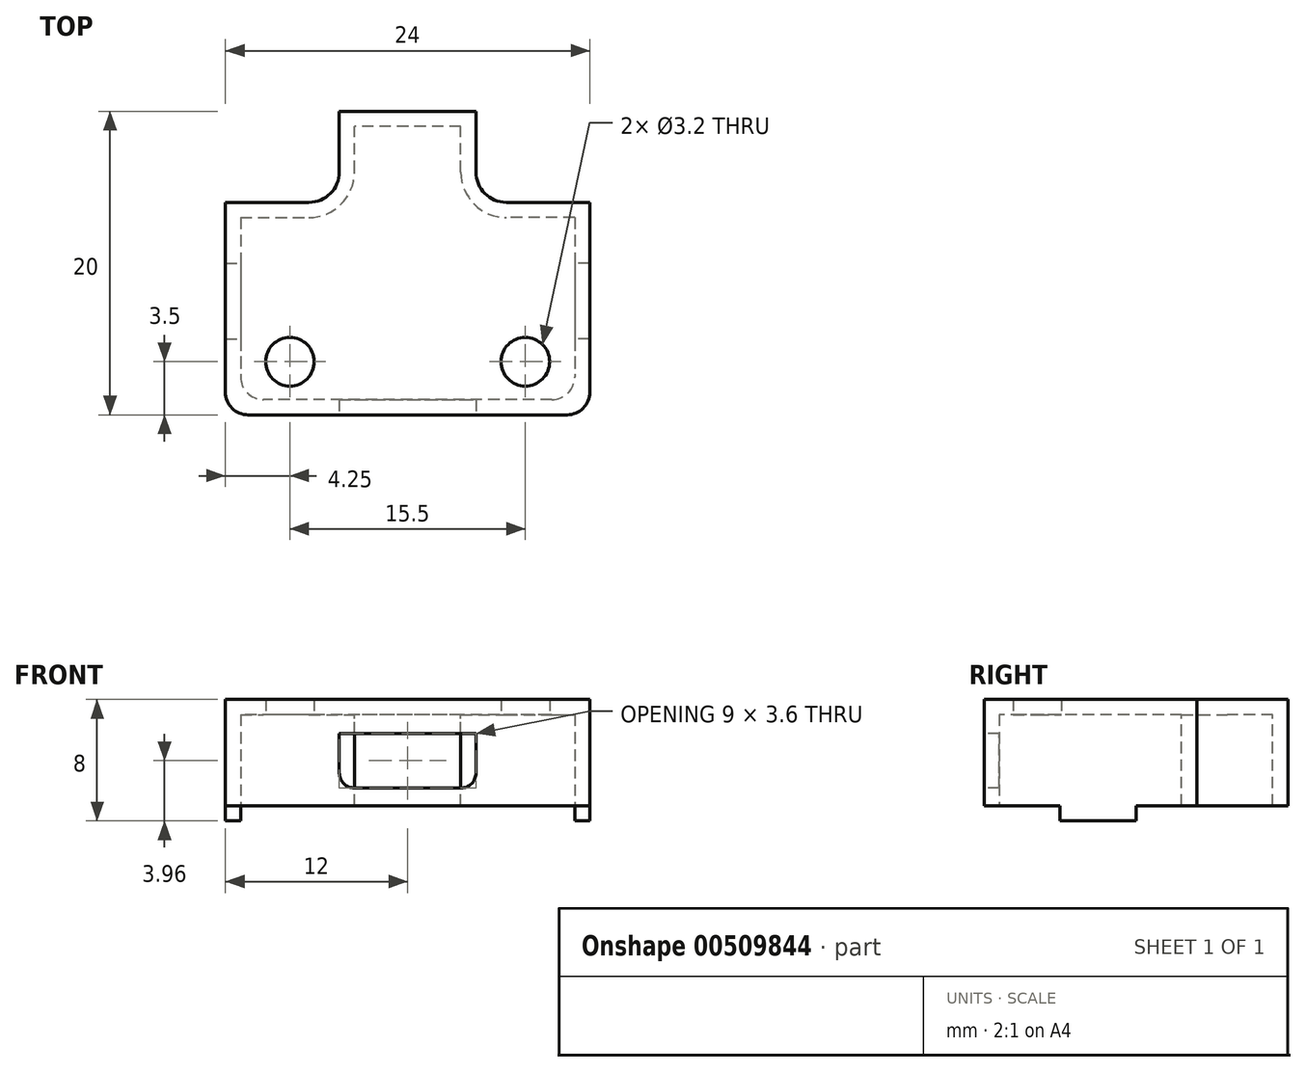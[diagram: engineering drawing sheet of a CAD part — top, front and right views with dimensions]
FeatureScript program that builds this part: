
annotation { "Feature Type Name" : "Feature", "Feature Type Description" : "" }
export const myFeature = defineFeature(function(context is Context, id is Id, definition is map)
    precondition{}
    {
        {
            var Q0;
            Q0=qCreatedBy(makeId("Top.planeOp"),FACE);
            var sketch = newSketch(context, id + "F0", { "sketchPlane" : qUnion([Q0])});
            skLineSegment(sketch, "E0.bottom", {"start": v(12, 2.5) * mm, "end": v(-12, 2.5) * mm});
            skLineSegment(sketch, "E0.top", {"start": v(12, -2.5) * mm, "end": v(-12, -2.5) * mm});
            skLineSegment(sketch, "E0.left", {"start": v(12, 2.5) * mm, "end": v(12, -2.5) * mm});
            skLineSegment(sketch, "E0.right", {"start": v(-12, 2.5) * mm, "end": v(-12, -2.5) * mm});
            skPoint(sketch, "E0.middle", {"position": v(0, 0) * mm});
            skCircle(sketch, "E1", {"center": v(-7, 0) * mm, "radius": 1.7 * mm});
            skCircle(sketch, "E2", {"center": v(7, 0) * mm, "radius": 1.7 * mm});
            skPoint(sketch, "E3.center.orphan", {"position": v(-2.5, 0) * mm});
            skPoint(sketch, "E4.center.orphan", {"position": v(-0.83, 0) * mm});
            skPoint(sketch, "E5.center.orphan", {"position": v(0.83, 0) * mm});
            skPoint(sketch, "E6.center.orphan", {"position": v(2.5, 0) * mm});
            skSolve(sketch);
        }
        {
            var Q0;
            Q0=qSketchRegion(id+"F0",true);
            extrude(context, id + "F1", {"entities" : qUnion([Q0]), "depth" : 7 * mm});
        }
        {
            var Q0;
            Q0=makeQuery(id+"F1.opExtrude","SWEPT_FACE",FACE,{"disambiguationData":[OSD([sQuery(id+"F0.wireOp",EDGE,"E0.top")])]});
            var sketch = newSketch(context, id + "F2", { "sketchPlane" : qUnion([Q0])});
            skLineSegment(sketch, "E7.bottom", {"start": v(-12, 7) * mm, "end": v(12, 7) * mm});
            skLineSegment(sketch, "E7.top", {"start": v(-12, 0) * mm, "end": v(12, 0) * mm});
            skLineSegment(sketch, "E7.left", {"start": v(-12, 7) * mm, "end": v(-12, 0) * mm});
            skLineSegment(sketch, "E7.right", {"start": v(12, 7) * mm, "end": v(12, 0) * mm});
            skSolve(sketch);
        }
        {
            var Q0;
            Q0=qSketchRegion(id+"F2",true);
            extrude(context, id + "F3", {"entities" : qUnion([Q0]), "operationType" : NewBodyOperationType.ADD, "depth" : 15 * mm});
        }
        {
            var Q0;
            Q0=makeQuery(id+"F3.boolean.opBoolean","MERGE",FACE,{"derivedFrom":[makeQuery(id+"F1.opExtrude","CAP_FACE",FACE,{"disambiguationData":[OSD([sQuery(id+"F0.wireOp",EDGE,"E0.bottom"),sQuery(id+"F0.wireOp",EDGE,"E0.top"),sQuery(id+"F0.wireOp",EDGE,"E0.left"),sQuery(id+"F0.wireOp",EDGE,"E0.right"),sQuery(id+"F0.wireOp",EDGE,"E3"),sQuery(id+"F0.wireOp",EDGE,"E4"),sQuery(id+"F0.wireOp",EDGE,"E5"),sQuery(id+"F0.wireOp",EDGE,"E6"),sQuery(id+"F0.wireOp",EDGE,"E1"),sQuery(id+"F0.wireOp",EDGE,"E2")])],"isStart":true}),makeQuery(id+"F3.opExtrude","SWEPT_FACE",FACE,{"disambiguationData":[OSD([sQuery(id+"F2.wireOp",EDGE,"E7.top")])]})]});
            var sketch = newSketch(context, id + "F4", { "sketchPlane" : qUnion([Q0])});
            skCircle(sketch, "E8", {"center": v(-7.75, 14) * mm, "radius": 1.6 * mm});
            skCircle(sketch, "E9", {"center": v(7.75, 14) * mm, "radius": 1.6 * mm});
            skSolve(sketch);
        }
        {
            var Q0;
            Q0=qSketchRegion(id+"F4",true);
            extrude(context, id + "F5", {"entities" : qUnion([Q0]), "operationType" : NewBodyOperationType.REMOVE, "oppositeDirection" : true, "depth" : 25 * mm});
        }
        {
            var Q0;
            Q0=makeQuery(id+"F3.boolean.opBoolean","MERGE",FACE,{"derivedFrom":[makeQuery(id+"F1.opExtrude","CAP_FACE",FACE,{"disambiguationData":[OSD([sQuery(id+"F0.wireOp",EDGE,"E0.bottom"),sQuery(id+"F0.wireOp",EDGE,"E0.top"),sQuery(id+"F0.wireOp",EDGE,"E0.left"),sQuery(id+"F0.wireOp",EDGE,"E0.right"),sQuery(id+"F0.wireOp",EDGE,"E3"),sQuery(id+"F0.wireOp",EDGE,"E4"),sQuery(id+"F0.wireOp",EDGE,"E5"),sQuery(id+"F0.wireOp",EDGE,"E6"),sQuery(id+"F0.wireOp",EDGE,"E1"),sQuery(id+"F0.wireOp",EDGE,"E2")])],"isStart":false}),makeQuery(id+"F3.opExtrude","SWEPT_FACE",FACE,{"disambiguationData":[OSD([sQuery(id+"F2.wireOp",EDGE,"E7.bottom")])]})]});
            var sketch = newSketch(context, id + "F6", { "sketchPlane" : qUnion([Q0])});
            skLineSegment(sketch, "E10", {"start": v(-12, 2.5) * mm, "end": v(-4.5, 2.5) * mm});
            skLineSegment(sketch, "E11", {"start": v(-12, 2.5) * mm, "end": v(-12, -3.5) * mm});
            skLineSegment(sketch, "E12", {"start": v(12, 2.5) * mm, "end": v(4.5, 2.5) * mm});
            skLineSegment(sketch, "E13", {"start": v(12, 2.5) * mm, "end": v(12, -3.5) * mm});
            skLineSegment(sketch, "E14", {"start": v(4.5, 2.5) * mm, "end": v(4.5, -1.5) * mm});
            skLineSegment(sketch, "E15", {"start": v(6.5, -3.5) * mm, "end": v(12, -3.5) * mm});
            skLineSegment(sketch, "E16", {"start": v(-4.5, 2.5) * mm, "end": v(-4.5, -1.5) * mm});
            skLineSegment(sketch, "E17", {"start": v(-6.5, -3.5) * mm, "end": v(-12, -3.5) * mm});
            skPoint(sketch, "E18.visualSharp", {"position": v(4.5, -3.5) * mm});
            skArc(sketch, "E18.filletArc", {"start": v(4.5, -1.5) * mm, "mid": v(5.09, -2.91) * mm, "end": v(6.5, -3.5) * mm});
            skPoint(sketch, "E19.visualSharp", {"position": v(-4.5, -3.5) * mm});
            skArc(sketch, "E19.filletArc", {"start": v(-6.5, -3.5) * mm, "mid": v(-5.09, -2.91) * mm, "end": v(-4.5, -1.5) * mm});
            skPoint(sketch, "E20.visualSharp", {"position": v(12, -3.5) * mm});
            skSolve(sketch);
        }
        {
            var Q0;
            Q0 = qSketchRegion(id + "F6", true);
            var Q1;
            Q1=makeQuery(id+"F3.boolean.opBoolean","MERGE",FACE,{"derivedFrom":[makeQuery(id+"F1.opExtrude","CAP_FACE",FACE,{"disambiguationData":[OSD([sQuery(id+"F0.wireOp",EDGE,"E0.bottom"),sQuery(id+"F0.wireOp",EDGE,"E0.top"),sQuery(id+"F0.wireOp",EDGE,"E0.left"),sQuery(id+"F0.wireOp",EDGE,"E0.right"),sQuery(id+"F0.wireOp",EDGE,"E3"),sQuery(id+"F0.wireOp",EDGE,"E4"),sQuery(id+"F0.wireOp",EDGE,"E5"),sQuery(id+"F0.wireOp",EDGE,"E6"),sQuery(id+"F0.wireOp",EDGE,"E1"),sQuery(id+"F0.wireOp",EDGE,"E2")])],"isStart":true}),makeQuery(id+"F3.opExtrude","SWEPT_FACE",FACE,{"disambiguationData":[OSD([sQuery(id+"F2.wireOp",EDGE,"E7.top")])]})]});
            extrude(context, id + "F7", {"entities" : qUnion([Q0]), "operationType" : NewBodyOperationType.REMOVE, "endBound" : BoundingType.UP_TO_SURFACE, "oppositeDirection" : true, "endBoundEntityFace" : qUnion([Q1]), "depth" : 25 * mm});
        }
        {
            var Q0;
            Q0=makeQuery(id+"F3.boolean.opBoolean","MERGE",FACE,{"derivedFrom":[makeQuery(id+"F1.opExtrude","CAP_FACE",FACE,{"disambiguationData":[OSD([sQuery(id+"F0.wireOp",EDGE,"E0.bottom"),sQuery(id+"F0.wireOp",EDGE,"E0.top"),sQuery(id+"F0.wireOp",EDGE,"E0.left"),sQuery(id+"F0.wireOp",EDGE,"E0.right"),sQuery(id+"F0.wireOp",EDGE,"E1"),sQuery(id+"F0.wireOp",EDGE,"E2")])],"isStart":true}),makeQuery(id+"F3.opExtrude","SWEPT_FACE",FACE,{"disambiguationData":[OSD([sQuery(id+"F2.wireOp",EDGE,"E7.top")])]})]});
            shell(context, id + "F8", {"entities" : qUnion([Q0]), "thickness" : 1 * mm});
        }
        {
            var Q0;
            Q0=makeQuery(id+"F3.boolean.opBoolean","MERGE",FACE,{"derivedFrom":[makeQuery(id+"F1.opExtrude","CAP_FACE",FACE,{"disambiguationData":[OSD([sQuery(id+"F0.wireOp",EDGE,"E0.bottom"),sQuery(id+"F0.wireOp",EDGE,"E0.top"),sQuery(id+"F0.wireOp",EDGE,"E0.left"),sQuery(id+"F0.wireOp",EDGE,"E0.right"),sQuery(id+"F0.wireOp",EDGE,"E1"),sQuery(id+"F0.wireOp",EDGE,"E2")])],"isStart":true}),makeQuery(id+"F3.opExtrude","SWEPT_FACE",FACE,{"disambiguationData":[OSD([sQuery(id+"F2.wireOp",EDGE,"E7.top")])]})]});
            var sketch = newSketch(context, id + "F9", { "sketchPlane" : qUnion([Q0])});
            skLineSegment(sketch, "E21.bottom", {"start": v(-11, 16.5) * mm, "end": v(11, 16.5) * mm});
            skLineSegment(sketch, "E21.top", {"start": v(-11, 10.87) * mm, "end": v(11, 10.87) * mm});
            skLineSegment(sketch, "E21.left", {"start": v(-11, 16.5) * mm, "end": v(-11, 10.87) * mm});
            skLineSegment(sketch, "E21.right", {"start": v(11, 16.5) * mm, "end": v(11, 10.87) * mm});
            skSolve(sketch);
        }
        {
            var Q0;
            Q0 = qSketchRegion(id + "F9", true);
            var Q1;
            Q1=makeQuery(id+"F8.opShell","OFFSET_FACE",FACE,{"disambiguationData":[OSD([sQuery(id+"F0.wireOp",EDGE,"E0.bottom"),sQuery(id+"F0.wireOp",EDGE,"E0.top"),sQuery(id+"F0.wireOp",EDGE,"E0.left"),sQuery(id+"F0.wireOp",EDGE,"E0.right"),sQuery(id+"F0.wireOp",EDGE,"E1"),sQuery(id+"F0.wireOp",EDGE,"E2"),sQuery(id+"F2.wireOp",EDGE,"E7.bottom")])]});
            extrude(context, id + "F10", {"entities" : qUnion([Q0]), "operationType" : NewBodyOperationType.REMOVE, "endBound" : BoundingType.UP_TO_SURFACE, "oppositeDirection" : true, "endBoundEntityFace" : qUnion([Q1]), "depth" : 25 * mm});
        }
        {
            var Q0;
            Q0=makeQuery(id+"F3.opExtrude","CAP_FACE",FACE,{"disambiguationData":[OSD([sQuery(id+"F2.wireOp",EDGE,"E7.bottom"),sQuery(id+"F2.wireOp",EDGE,"E7.top"),sQuery(id+"F2.wireOp",EDGE,"E7.left"),sQuery(id+"F2.wireOp",EDGE,"E7.right")])],"isStart":false});
            var sketch = newSketch(context, id + "F11", { "sketchPlane" : qUnion([Q0])});
            skLineSegment(sketch, "E22.bottom", {"start": v(4.5, 4.76) * mm, "end": v(-4.5, 4.76) * mm});
            skLineSegment(sketch, "E22.top", {"start": v(4.5, 1.16) * mm, "end": v(-4.5, 1.16) * mm});
            skLineSegment(sketch, "E22.left", {"start": v(4.5, 4.76) * mm, "end": v(4.5, 1.16) * mm});
            skLineSegment(sketch, "E22.right", {"start": v(-4.5, 4.76) * mm, "end": v(-4.5, 1.16) * mm});
            skPoint(sketch, "E22.middle", {"position": v(0, 2.96) * mm});
            skSolve(sketch);
        }
        {
            var Q0;
            Q0 = qSketchRegion(id + "F11", true);
            var Q1;
            {var subQ0=sQuery(id+"F2.wireOp",EDGE,"E7.right");var subQ1=sQuery(id+"F2.wireOp",EDGE,"E7.left");var subQ2=sQuery(id+"F2.wireOp",EDGE,"E7.top");var subQ3=sQuery(id+"F2.wireOp",EDGE,"E7.bottom");Q1=makeQuery(id+"F10.boolean.opBoolean","MERGE",FACE,{"derivedFrom":[makeQuery(id+"F8.opShell","OFFSET_FACE",FACE,{"disambiguationData":[OSD([subQ3,subQ2,subQ1,subQ0]),OD(0.0)]}),makeQuery(id+"F8.opShell","OFFSET_FACE",FACE,{"disambiguationData":[OSD([subQ3,subQ2,subQ1,subQ0]),OD(1.0)]}),makeQuery(id+"F8.opShell","OFFSET_FACE",FACE,{"disambiguationData":[OSD([subQ3,subQ2,subQ1,subQ0]),OD(2.0)]}),makeQuery(id+"F10.opExtrude","SWEPT_FACE",FACE,{"disambiguationData":[OSD([sQuery(id+"F9.wireOp",EDGE,"E21.bottom")])]})]});}
            extrude(context, id + "F12", {"entities" : qUnion([Q0]), "operationType" : NewBodyOperationType.REMOVE, "endBound" : BoundingType.UP_TO_SURFACE, "oppositeDirection" : true, "endBoundEntityFace" : qUnion([Q1]), "depth" : 25 * mm});
        }
        {
            var Q0;
            Q0=makeQuery(id+"F12.boolean.opBoolean","COPY",EDGE,{"derivedFrom":makeQuery(id+"F12.opExtrude","SWEPT_EDGE",EDGE,{"disambiguationData":[OSD([sQuery(id+"F11.wireOp",EDGE,"E22.top"),sQuery(id+"F11.wireOp",EDGE,"E22.right")])]})});
            var Q1;
            Q1=makeQuery(id+"F12.boolean.opBoolean","COPY",EDGE,{"derivedFrom":makeQuery(id+"F12.opExtrude","SWEPT_EDGE",EDGE,{"disambiguationData":[OSD([sQuery(id+"F11.wireOp",EDGE,"E22.top"),sQuery(id+"F11.wireOp",EDGE,"E22.left")])]})});
            fillet(context, id + "F13", {"entities" : qUnion([Q0, Q1]), "radius" : 1 * mm, "tangentPropagation" : true, "allowEdgeOverflow" : false});
        }
        {
            var Q0;
            Q0=makeQuery(id+"F3.opExtrude","CAP_EDGE",EDGE,{"disambiguationData":[OSD([sQuery(id+"F2.wireOp",EDGE,"E7.right")])],"isStart":false});
            var Q1;
            Q1=makeQuery(id+"F8.opShell","OFFSET_EDGE",EDGE,{"disambiguationData":[OSD([sQuery(id+"F2.wireOp",EDGE,"E7.right")])]});
            var Q2;
            Q2=makeQuery(id+"F8.opShell","OFFSET_EDGE",EDGE,{"disambiguationData":[OSD([sQuery(id+"F2.wireOp",EDGE,"E7.left")])]});
            var Q3;
            Q3=makeQuery(id+"F3.opExtrude","CAP_EDGE",EDGE,{"disambiguationData":[OSD([sQuery(id+"F2.wireOp",EDGE,"E7.left")])],"isStart":false});
            fillet(context, id + "F14", {"entities" : qUnion([Q0, Q1, Q2, Q3]), "radius" : 1.5 * mm, "tangentPropagation" : true, "allowEdgeOverflow" : false});
        }
        {
            var Q0;
            Q0=makeQuery(id+"F3.boolean.opBoolean","MERGE",FACE,{"derivedFrom":[makeQuery(id+"F1.opExtrude","CAP_FACE",FACE,{"disambiguationData":[OSD([sQuery(id+"F0.wireOp",EDGE,"E0.bottom"),sQuery(id+"F0.wireOp",EDGE,"E0.top"),sQuery(id+"F0.wireOp",EDGE,"E0.left"),sQuery(id+"F0.wireOp",EDGE,"E0.right"),sQuery(id+"F0.wireOp",EDGE,"E1"),sQuery(id+"F0.wireOp",EDGE,"E2")])],"isStart":true}),makeQuery(id+"F3.opExtrude","SWEPT_FACE",FACE,{"disambiguationData":[OSD([sQuery(id+"F2.wireOp",EDGE,"E7.top")])]})]});
            var sketch = newSketch(context, id + "F15", { "sketchPlane" : qUnion([Q0])});
            skLineSegment(sketch, "E23.bottom", {"start": v(12, 7.5) * mm, "end": v(11, 7.5) * mm});
            skLineSegment(sketch, "E23.top", {"start": v(12, 12.5) * mm, "end": v(11, 12.5) * mm});
            skLineSegment(sketch, "E23.left", {"start": v(12, 7.5) * mm, "end": v(12, 12.5) * mm});
            skLineSegment(sketch, "E23.right", {"start": v(11, 7.5) * mm, "end": v(11, 12.5) * mm});
            skLineSegment(sketch, "E24.bottom", {"start": v(-12, 7.5) * mm, "end": v(-11, 7.5) * mm});
            skLineSegment(sketch, "E24.top", {"start": v(-12, 12.5) * mm, "end": v(-11, 12.5) * mm});
            skLineSegment(sketch, "E24.left", {"start": v(-12, 7.5) * mm, "end": v(-12, 12.5) * mm});
            skLineSegment(sketch, "E24.right", {"start": v(-11, 7.5) * mm, "end": v(-11, 12.5) * mm});
            skSolve(sketch);
        }
        {
            var Q0;
            Q0 = qSketchRegion(id + "F15", true);
            extrude(context, id + "F16", {"entities" : qUnion([Q0]), "operationType" : NewBodyOperationType.ADD, "depth" : 1 * mm});
        }
    });
